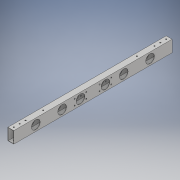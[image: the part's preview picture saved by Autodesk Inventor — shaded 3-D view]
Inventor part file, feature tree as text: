
AUTODESK INVENTOR PART (.ipt)
format: ipt  version: 2018 (Build 220112000, 112)  size: 195,072 bytes
history: native  units: in
note: dims shown in document units (in); Inventor stores cm internally (conversion verified against a paired STEP export)
features: extrude x4, sketch x4
ambient origin geometry x8: Origin, YZ Plane, XZ Plane, XY Plane, X Axis, Y Axis, Z Axis, Center Point
bodies: Solid1 (feature_tree)
feature tree (8):
  extrude  "Extrusion1"  Depth=2.0in
  extrude  "Extrusion2"  Depth=27.0in TaperAngle=0.0deg
  extrude  "Extrusion5"  Depth=8.25in
  extrude  "Extrusion6"  Depth=1.0in
  sketch  "Sketch1"  dims[d0=1.0in d1=2.0in]
  sketch  "Sketch2"  dims[d2=0.0625in d3=27.0in d4=0.0in]
  sketch  "Sketch3"  dims[d5=3.75in d6=8.25in]
  sketch  "Sketch4"  dims[d7=11.375in d8=1.5in d9=1.5in d10=1.5in d11=27.0in d12=0.0in d13=1.5in d14=1.0in d15=3.0in d16=1.5in d17=1.0in d18=3.0in d19=0.2031in d24=0.5in d25=0.5in d26=8.5in d27=0.0in d28=10.371in d29=0.506in d30=1.0in d31=2.0in d32=1.0in d33=0.203in d34=8.5in d35=0.0in]
